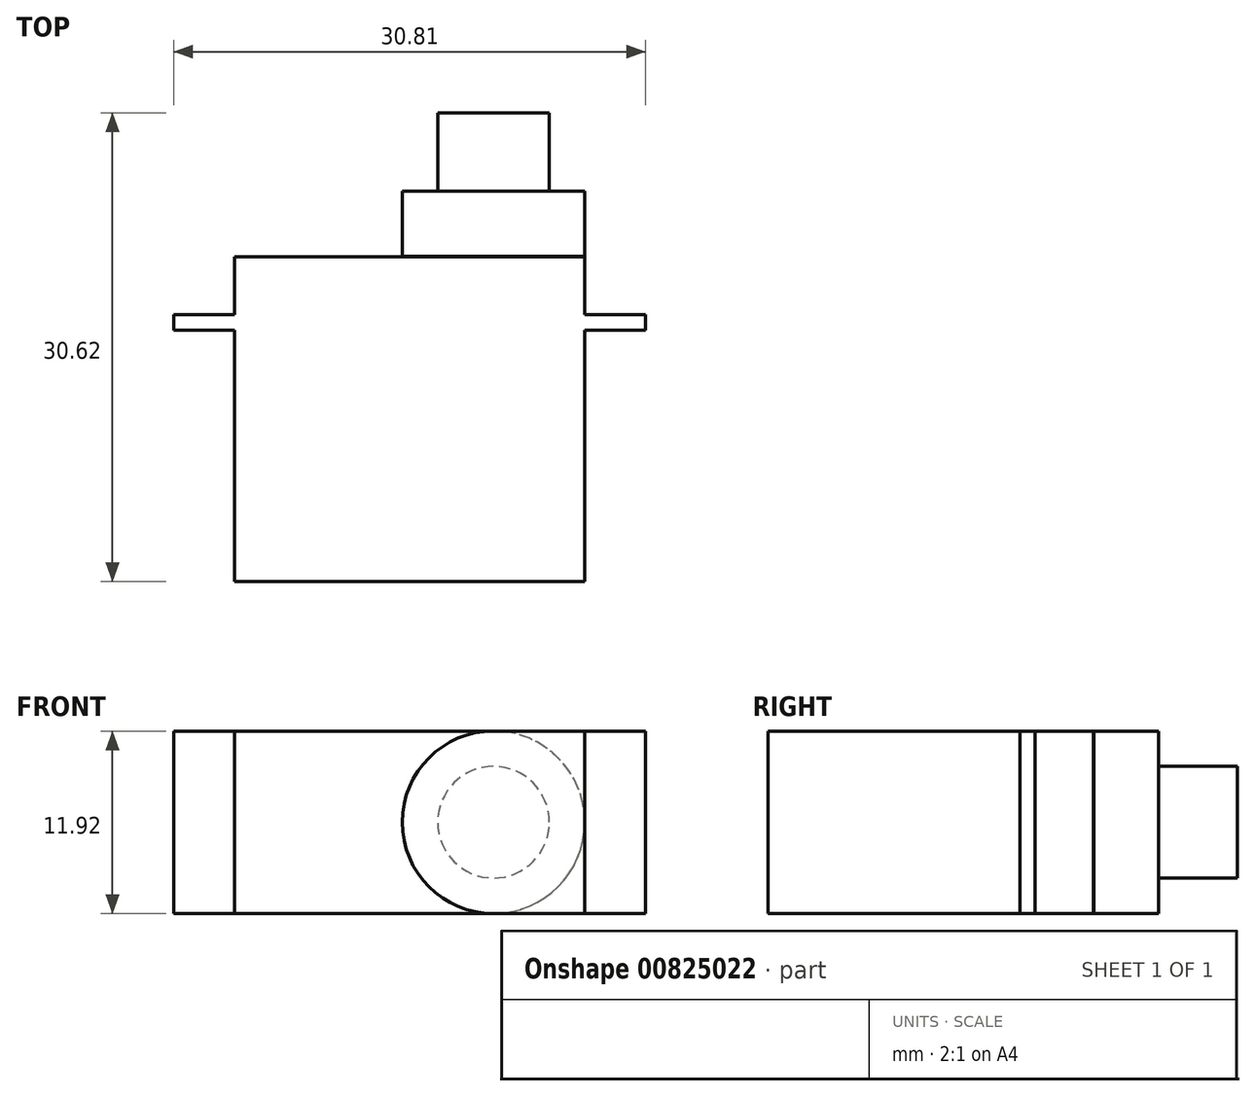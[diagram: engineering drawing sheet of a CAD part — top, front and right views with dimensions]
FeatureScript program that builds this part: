
annotation { "Feature Type Name" : "Feature", "Feature Type Description" : "" }
export const myFeature = defineFeature(function(context is Context, id is Id, definition is map)
    precondition{}
    {
        {
            var Q0;
            Q0=qCreatedBy(makeId("Top.planeOp"),FACE);
            var sketch = newSketch(context, id + "F0", { "sketchPlane" : qUnion([Q0])});
            skLineSegment(sketch, "E0", {"start": v(-59.86, 12.93) * mm, "end": v(-59.86, -8.3) * mm});
            skLineSegment(sketch, "E1", {"start": v(-59.86, -8.3) * mm, "end": v(-36.99, -8.3) * mm});
            skLineSegment(sketch, "E2", {"start": v(-36.99, -8.3) * mm, "end": v(-36.99, 12.93) * mm});
            skLineSegment(sketch, "E3", {"start": v(-36.99, 12.93) * mm, "end": v(-59.86, 12.93) * mm});
            skLineSegment(sketch, "E4", {"start": v(-59.86, 9.13) * mm, "end": v(-36.99, 9.13) * mm});
            skLineSegment(sketch, "E5", {"start": v(-59.86, 8.13) * mm, "end": v(-36.99, 8.13) * mm});
            skLineSegment(sketch, "E6", {"start": v(-36.99, 9.13) * mm, "end": v(-33.02, 9.13) * mm});
            skLineSegment(sketch, "E7", {"start": v(-33.02, 9.13) * mm, "end": v(-33.02, 8.13) * mm});
            skLineSegment(sketch, "E8", {"start": v(-33.02, 8.13) * mm, "end": v(-36.99, 8.13) * mm});
            skLineSegment(sketch, "E9", {"start": v(-59.86, 9.13) * mm, "end": v(-63.83, 9.13) * mm});
            skLineSegment(sketch, "E10", {"start": v(-63.83, 9.13) * mm, "end": v(-63.83, 8.13) * mm});
            skLineSegment(sketch, "E11", {"start": v(-63.83, 8.13) * mm, "end": v(-59.86, 8.13) * mm});
            skSolve(sketch);
        }
        {
            var Q0;
            Q0=qCreatedBy(makeId("Front.planeOp"),FACE);
            cPlane(context, id + "F1", {"entities" : qUnion([Q0]), "cplaneType" : CPlaneType.OFFSET, "offset" : 12.95 * mm, "oppositeDirection" : true, "width" : 152.4 * mm, "height" : 152.4 * mm});
        }
        {
            var Q0;
            Q0=qCreatedBy(id+"F1.planeOp",FACE);
            var sketch = newSketch(context, id + "F2", { "sketchPlane" : qUnion([Q0])});
            skLineSegment(sketch, "E12", {"start": v(-36.99, 0) * mm, "end": v(-36.99, -11.92) * mm});
            skLineSegment(sketch, "E13", {"start": v(-36.99, -11.92) * mm, "end": v(-59.86, -11.92) * mm});
            skLineSegment(sketch, "E14", {"start": v(-59.86, -11.92) * mm, "end": v(-59.86, 0) * mm});
            skLineSegment(sketch, "E15", {"start": v(-59.86, 0) * mm, "end": v(-36.99, 0) * mm});
            skCircle(sketch, "E16", {"center": v(-42.95, -5.96) * mm, "radius": 5.96 * mm});
            skPoint(sketch, "E17", {"position": v(-42.95, 0) * mm});
            skPoint(sketch, "E18", {"position": v(-36.99, -5.96) * mm});
            skPoint(sketch, "E19", {"position": v(-42.95, -11.92) * mm});
            skCircle(sketch, "E20", {"center": v(-42.95, -5.96) * mm, "radius": 3.64 * mm});
            skSolve(sketch);
        }
        {
            var Q0;
            {var subQ0=sQuery(id+"F0.wireOp",EDGE,"E3");Q0=makeQuery(id+"F0.imprint","IMPRINT",FACE,{"disambiguationData":[TD([[makeQuery(id+"F0.imprint","IMPRINT",EDGE,{"derivedFrom":subQ0}),1.0]])]});}
            var Q1;
            {var subQ0=sQuery(id+"F0.wireOp",EDGE,"E4");Q1=makeQuery(id+"F0.imprint","IMPRINT",FACE,{"disambiguationData":[TD([[makeQuery(id+"F0.imprint","IMPRINT",EDGE,{"derivedFrom":subQ0}),-1.0]])]});}
            var Q2;
            {var subQ0=sQuery(id+"F0.wireOp",EDGE,"E6");Q2=makeQuery(id+"F0.imprint","IMPRINT",FACE,{"disambiguationData":[TD([[makeQuery(id+"F0.imprint","IMPRINT",EDGE,{"derivedFrom":subQ0}),-1.0]])]});}
            var Q3;
            {var subQ0=sQuery(id+"F0.wireOp",EDGE,"E9");Q3=makeQuery(id+"F0.imprint","IMPRINT",FACE,{"disambiguationData":[TD([[makeQuery(id+"F0.imprint","IMPRINT",EDGE,{"derivedFrom":subQ0}),1.0]])]});}
            var Q4;
            {var subQ0=sQuery(id+"F0.wireOp",EDGE,"E1");Q4=makeQuery(id+"F0.imprint","IMPRINT",FACE,{"disambiguationData":[TD([[makeQuery(id+"F0.imprint","IMPRINT",EDGE,{"derivedFrom":subQ0}),1.0]])]});}
            extrude(context, id + "F3", {"entities" : qUnion([Q0, Q1, Q2, Q3, Q4]), "oppositeDirection" : true, "depth" : 11.92 * mm, "offsetDistance" : 25.4 * mm});
        }
        {
            var Q0;
            Q0=makeQuery(id+"F2.imprint","IMPRINT",FACE,{"disambiguationData":[TD([[makeQuery(id+"F2.imprint","IMPRINT",EDGE,{"derivedFrom":sQuery(id+"F2.wireOp",EDGE,"E20")}),1.0]])]});
            extrude(context, id + "F4", {"entities" : qUnion([Q0]), "oppositeDirection" : true, "depth" : 9.37 * mm, "offsetDistance" : 25.4 * mm});
        }
        {
            var Q0;
            Q0=makeQuery(id+"F2.imprint","IMPRINT",FACE,{"disambiguationData":[TD([[makeQuery(id+"F2.imprint","IMPRINT",EDGE,{"derivedFrom":sQuery(id+"F2.wireOp",EDGE,"E20")}),-1.0]])]});
            extrude(context, id + "F5", {"entities" : qUnion([Q0]), "operationType" : NewBodyOperationType.ADD, "oppositeDirection" : true, "depth" : 4.25 * mm, "offsetDistance" : 25.4 * mm});
        }
    });
